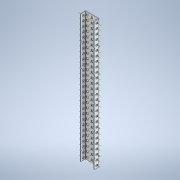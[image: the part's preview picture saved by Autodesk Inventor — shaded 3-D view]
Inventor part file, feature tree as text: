
AUTODESK INVENTOR PART (.ipt)
format: ipt  version: 2020 (Build 240168000, 168)  size: 1,373,184 bytes
history: native  units: in
note: dims shown in document units (in); Inventor stores cm internally (conversion verified against a paired STEP export)
features: other x138, plane x5, pattern_linear x3, split x1, sheet_metal_op x1
ambient origin geometry x8: Origin, YZ Plane, XZ Plane, XY Plane, X Axis, Y Axis, Z Axis, Center Point
bodies: Solid1 (feature_tree)
feature tree (148):
  plane  "Work Plane2"
  plane  "Work Plane1"
  other  "Work Point1"
  other  "Work Point2"
  other  "Work Axis1"
  other  "Work Axis2"
  other  "Work Axis3"
  pattern_linear  "Rectangular Pattern1"  Count1=27 Spacing1=0.5in
  pattern_linear  "Rectangular Pattern2"  Count1=27 Spacing1=0.5in
  pattern_linear  "Rectangular Pattern3"  Count1=27 Spacing1=0.5in
  plane  "Work Plane5"
  split  "Split1"
  plane  "Work Plane3"
  plane  "Work Plane4"
  other  "Work Point3"
  other  "Work Axis4"
  other  "Work Axis5"
  other  "Work Axis6"
  other  "Work Axis7"
  other  "Work Axis8"
  other  "Work Axis9"
  other  "Work Axis10"
  other  "Work Axis11"
  other  "Work Axis12"
  other  "Work Axis13"
  other  "Work Axis14"
  other  "Work Axis15"
  other  "Work Axis16"
  other  "Work Axis17"
  other  "Work Axis18"
  other  "Work Axis19"
  other  "Work Axis20"
  other  "Work Axis21"
  other  "Work Axis22"
  other  "Work Axis23"
  other  "Work Axis24"
  other  "Work Axis25"
  other  "Work Axis26"
  other  "Work Axis27"
  other  "Work Axis28"
  other  "Work Axis29"
  other  "Work Axis38"
  other  "Work Axis39"
  other  "Work Axis40"
  other  "Work Axis41"
  other  "Work Axis42"
  other  "Work Axis43"
  other  "Work Axis44"
  other  "Work Axis45"
  other  "Work Axis46"
  other  "Work Axis47"
  other  "Work Axis48"
  other  "Work Axis49"
  other  "Work Axis50"
  other  "Work Axis51"
  other  "Work Axis52"
  other  "Work Axis53"
  other  "Work Axis54"
  other  "Work Axis55"
  other  "Work Axis56"
  other  "Work Axis57"
  other  "Work Axis58"
  other  "Work Axis59"
  other  "Work Axis60"
  other  "Work Axis61"
  other  "Work Axis62"
  other  "Work Axis63"
  other  "Work Axis72"
  other  "Work Axis73"
  other  "Work Axis74"
  other  "Work Axis75"
  other  "Work Axis76"
  other  "Work Axis77"
  other  "Work Axis78"
  other  "Work Axis79"
  other  "Work Axis80"
  other  "Work Axis81"
  other  "Work Axis82"
  other  "Work Axis83"
  other  "Work Axis84"
  other  "Work Axis85"
  other  "Work Axis86"
  other  "Work Axis87"
  other  "Work Axis88"
  other  "Work Axis89"
  other  "Work Axis90"
  other  "Work Axis91"
  other  "Work Axis92"
  other  "Work Axis93"
  other  "Work Axis94"
  other  "Work Axis95"
  other  "Work Axis96"
  other  "Work Axis97"
  other  "Work Axis106"
  other  "Work Axis107"
  other  "Work Axis108"
  other  "Work Axis109"
  other  "Work Axis110"
  other  "Work Axis111"
  other  "Work Axis112"
  other  "Work Axis113"
  other  "Work Axis114"
  other  "Work Axis115"
  other  "Work Axis116"
  other  "Work Axis117"
  other  "Work Axis118"
  other  "Work Axis119"
  other  "Work Axis120"
  other  "Work Axis121"
  other  "Work Axis122"
  other  "Work Axis123"
  other  "Work Axis124"
  other  "Work Axis125"
  other  "Work Axis126"
  other  "Work Axis127"
  other  "Work Axis128"
  other  "Work Axis129"
  other  "Work Axis130"
  other  "Work Axis131"
  other  "Work Axis132"
  other  "Work Axis141"
  other  "Work Axis142"
  other  "Work Axis143"
  other  "Work Axis144"
  other  "Work Axis145"
  other  "Work Axis146"
  other  "Work Axis147"
  other  "Work Axis148"
  other  "Work Axis149"
  other  "Work Axis150"
  other  "Work Axis151"
  other  "Work Axis152"
  other  "Work Axis153"
  other  "Work Axis154"
  other  "Work Axis155"
  other  "Work Axis156"
  other  "Work Axis157"
  other  "Work Axis158"
  other  "Work Axis159"
  other  "Work Axis160"
  other  "Work Axis161"
  other  "Work Axis162"
  other  "Work Axis163"
  other  "Work Axis164"
  other  "Work Axis165"
  other  "Work Axis166"
  other  "Work Axis167"
  sheet_metal_op  "Fold1"
